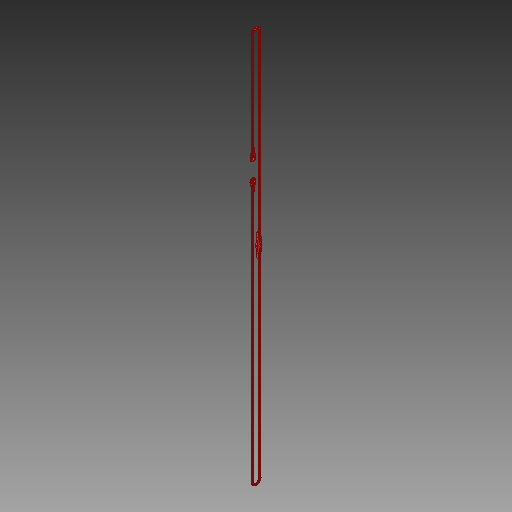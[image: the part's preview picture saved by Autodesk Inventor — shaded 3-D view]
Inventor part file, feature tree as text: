
AUTODESK INVENTOR PART (.ipt)
format: ipt  version: 2017 SP1 (Build 210196100, 196)  size: 314,368 bytes
history: native  units: in
note: dims shown in document units (in); Inventor stores cm internally (conversion verified against a paired STEP export)
features: extrude x1, fillet x1
ambient origin geometry x8: Origin, YZ Plane, XZ Plane, XY Plane, X Axis, Y Axis, Z Axis, Center Point
bodies: Solid1 (feature_tree)
feature tree (2):
  extrude  "Extrusion1"  Depth=0.375in
  fillet  "Fillet1"  Radius=0.1875in
